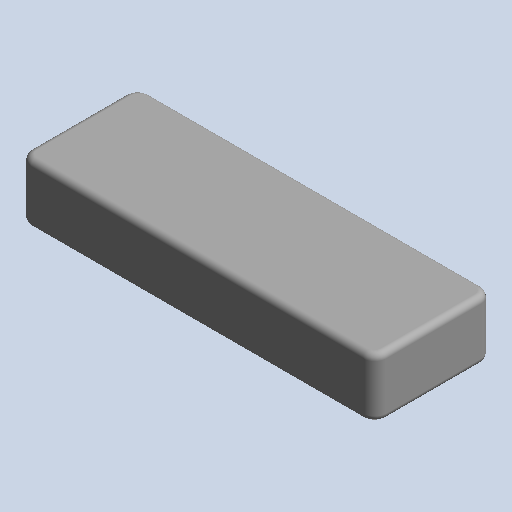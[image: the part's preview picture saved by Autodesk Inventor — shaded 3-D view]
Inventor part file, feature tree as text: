
AUTODESK INVENTOR PART (.ipt)
format: ipt  version: 2022.1 (Build 261234000, 234)  size: 70,144 bytes
history: native  units: mm (DEFAULTED — no unit token found)
features: other x8, fillet x1
bodies: Body1 (feature_tree)
feature tree (9):
  other  "Sólido1"
  other  "Origen"
  other  "Plano YZ"
  other  "Plano XZ"
  other  "Plano XY"
  other  "Eje X"
  other  "Eje Y"
  other  "Eje Z"
  fillet  "Fillet2"  [1 undecoded]
note: 1 required parameter value undecoded (feature->parameter linkage not recoverable at this tier; creation-order binding heuristic only, values carry confidence <= 0.55)
